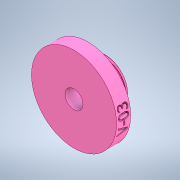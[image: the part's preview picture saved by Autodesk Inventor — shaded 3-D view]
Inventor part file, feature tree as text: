
AUTODESK INVENTOR PART (.ipt)
format: ipt  version: 2021.1 (Build 251245000, 245)  size: 570,368 bytes
history: native  units: in
note: dims shown in document units (in); Inventor stores cm internally (conversion verified against a paired STEP export)
features: sketch x4, extrude x2, helix x1, plane x1, emboss x1
ambient origin geometry x8: Origin, YZ Plane, XZ Plane, XY Plane, X Axis, Y Axis, Z Axis, Center Point
bodies: Solid1 (feature_tree)
feature tree (9):
  extrude  "Extrusion1"  Depth=1.6147in
  extrude  "Extrusion2"  Depth=3.0in
  helix  "Coil2"  [1 undecoded]
  plane  "Work Plane1"
  emboss  "Emboss1"
  sketch  "Sketch1"  dims[d0=0.635in d1=1.6147in]
  sketch  "Sketch2"  dims[d2=0.6in d3=0.0in d4=3.0in d5=0.5in d6=0.0in]
  sketch  "Sketch9"  dims[d38=60.0deg]
  sketch  "Sketch10"  dims[d39=0.0088in d41=0.0833in d42=0.8073in d43=0.0833in d44=0.7667in d45=0.3937in d46=0.0in d47=90.0deg d48=90.0deg d49=0.0in d50=0.0in d52=0.7555in d53=1.5in d54=0.1in d55=0.0in d56=0.635in d28=0.5in d29=0.0344in d30=0.5in d31=0.0344in]
note: 1 required parameter value undecoded (feature->parameter linkage not recoverable at this tier; creation-order binding heuristic only, values carry confidence <= 0.55)
